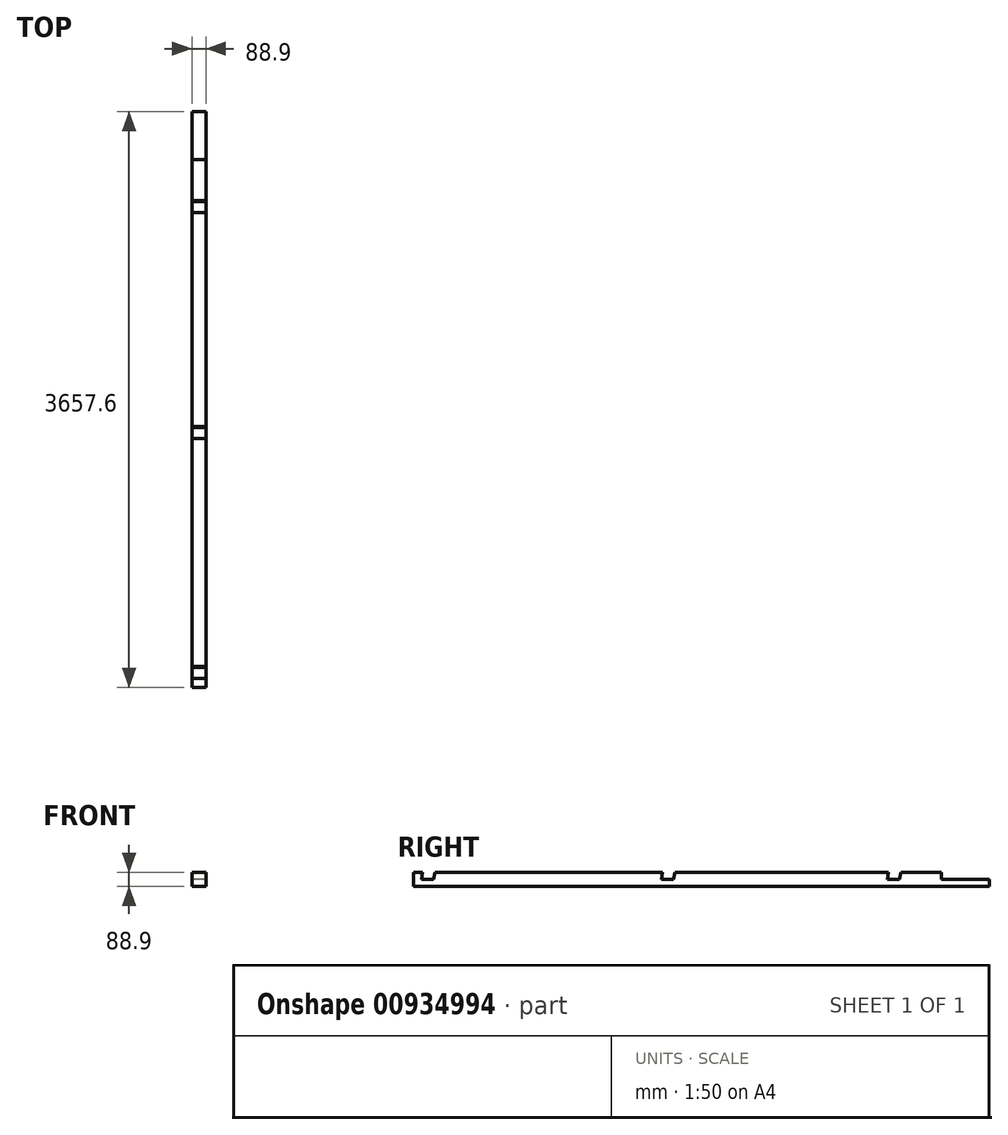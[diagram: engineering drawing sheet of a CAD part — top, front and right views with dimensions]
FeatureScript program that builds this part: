
annotation { "Feature Type Name" : "Feature", "Feature Type Description" : "" }
export const myFeature = defineFeature(function(context is Context, id is Id, definition is map)
    precondition{}
    {
        {
            var Q0;
            Q0=qCreatedBy(makeId("Front.planeOp"),FACE);
            var sketch = newSketch(context, id + "F0", { "sketchPlane" : qUnion([Q0])});
            skLineSegment(sketch, "E0.bottom", {"start": v(-44.45, 44.45) * mm, "end": v(44.45, 44.45) * mm});
            skLineSegment(sketch, "E0.top", {"start": v(-44.45, -44.45) * mm, "end": v(44.45, -44.45) * mm});
            skLineSegment(sketch, "E0.left", {"start": v(-44.45, 44.45) * mm, "end": v(-44.45, -44.45) * mm});
            skLineSegment(sketch, "E0.right", {"start": v(44.45, 44.45) * mm, "end": v(44.45, -44.45) * mm});
            skPoint(sketch, "E0.middle", {"position": v(0, 0) * mm});
            skSolve(sketch);
        }
        {
            var Q0;
            Q0 = qSketchRegion(id + "F0", true);
            extrude(context, id + "F1", {"entities" : qUnion([Q0]), "depth" : 3657.6 * mm, "offsetDistance" : 25.4 * mm});
        }
        {
            var Q0;
            Q0=qCreatedBy(makeId("Right.planeOp"),FACE);
            var sketch = newSketch(context, id + "F2", { "sketchPlane" : qUnion([Q0])});
            skLineSegment(sketch, "E1.bottom", {"start": v(-304.8, 44.45) * mm, "end": v(0, 44.45) * mm});
            skLineSegment(sketch, "E1.top", {"start": v(-304.8, 0) * mm, "end": v(0, 0) * mm});
            skLineSegment(sketch, "E1.left", {"start": v(-304.8, 44.45) * mm, "end": v(-304.8, 0) * mm});
            skLineSegment(sketch, "E1.right", {"start": v(0, 44.45) * mm, "end": v(0, 0) * mm});
            skLineSegment(sketch, "E2", {"start": v(-3600.45, 44.45) * mm, "end": v(-3607.63, 0.58) * mm});
            skLineSegment(sketch, "E3", {"start": v(-3607.63, 0.58) * mm, "end": v(-3530.42, 0.58) * mm});
            skLineSegment(sketch, "E4", {"start": v(-3530.42, 0.58) * mm, "end": v(-3523.24, 44.45) * mm});
            skLineSegment(sketch, "E5", {"start": v(-3523.24, 44.45) * mm, "end": v(-3600.45, 44.45) * mm});
            skLineSegment(sketch, "E6", {"start": v(-2076.45, 44.45) * mm, "end": v(-2083.63, 0.58) * mm});
            skLineSegment(sketch, "E7", {"start": v(-2083.63, 0.58) * mm, "end": v(-2006.42, 0.58) * mm});
            skLineSegment(sketch, "E8", {"start": v(-2006.42, 0.58) * mm, "end": v(-1999.24, 44.45) * mm});
            skLineSegment(sketch, "E9", {"start": v(-1999.24, 44.45) * mm, "end": v(-2076.45, 44.45) * mm});
            skLineSegment(sketch, "E10", {"start": v(-641.35, 44.45) * mm, "end": v(-648.53, 0.58) * mm});
            skLineSegment(sketch, "E11", {"start": v(-648.53, 0.58) * mm, "end": v(-571.32, 0.58) * mm});
            skLineSegment(sketch, "E12", {"start": v(-571.32, 0.58) * mm, "end": v(-564.14, 44.45) * mm});
            skLineSegment(sketch, "E13", {"start": v(-564.14, 44.45) * mm, "end": v(-641.35, 44.45) * mm});
            skSolve(sketch);
        }
        {
            var Q0;
            Q0 = qSketchRegion(id + "F2", true);
            extrude(context, id + "F3", {"entities" : qUnion([Q0]), "operationType" : NewBodyOperationType.REMOVE, "depth" : 254 * mm, "offsetDistance" : 25.4 * mm, "symmetric" : true});
        }
    });
